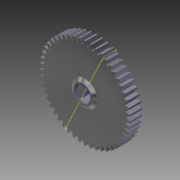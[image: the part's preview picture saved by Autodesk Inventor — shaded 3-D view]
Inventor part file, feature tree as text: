
AUTODESK INVENTOR PART (.ipt)
format: ipt  version: 2016 SP1 (Build 200210100, 210)  size: 424,448 bytes
history: native  units: in
note: dims shown in document units (in); Inventor stores cm internally (conversion verified against a paired STEP export)
features: plane x1, imported_body x1
ambient origin geometry x8: Origin, YZ Plane, XZ Plane, XY Plane, X Axis, Y Axis, Z Axis, Center Point
bodies: Solid1 (feature_tree)
feature tree (2):
  plane  "Work Plane2"
  imported_body  "Imported1"
